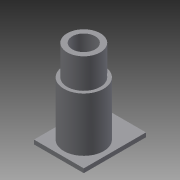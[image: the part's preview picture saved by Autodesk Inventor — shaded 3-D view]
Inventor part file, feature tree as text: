
AUTODESK INVENTOR PART (.ipt)
format: ipt  version: 2014 (Build 180170000, 170)  size: 102,912 bytes
history: native  units: in
note: dims shown in document units (in); Inventor stores cm internally (conversion verified against a paired STEP export)
features: extrude x4, sketch x4
ambient origin geometry x8: Origin, YZ Plane, XZ Plane, XY Plane, X Axis, Y Axis, Z Axis, Center Point
bodies: Solid1 (feature_tree)
feature tree (8):
  extrude  "Extrusion1"  Depth=0.275in
  extrude  "Extrusion2"  Depth=0.6in
  extrude  "Extrusion3"  Depth=0.1in TaperAngle=0.0deg
  extrude  "Extrusion4"  Depth=0.6in
  sketch  "Sketch1"  dims[d0=0.48in d1=0.275in]
  sketch  "Sketch2"  dims[d2=0.6in d3=0.0in d4=0.4in]
  sketch  "Sketch3"  dims[d5=0.36in d6=0.0in d7=0.1in d8=0.0in]
  sketch  "Sketch4"  dims[d10=0.05in d11=0.0in d12=0.6in d13=0.75in d14=0.3in d15=0.3in]
